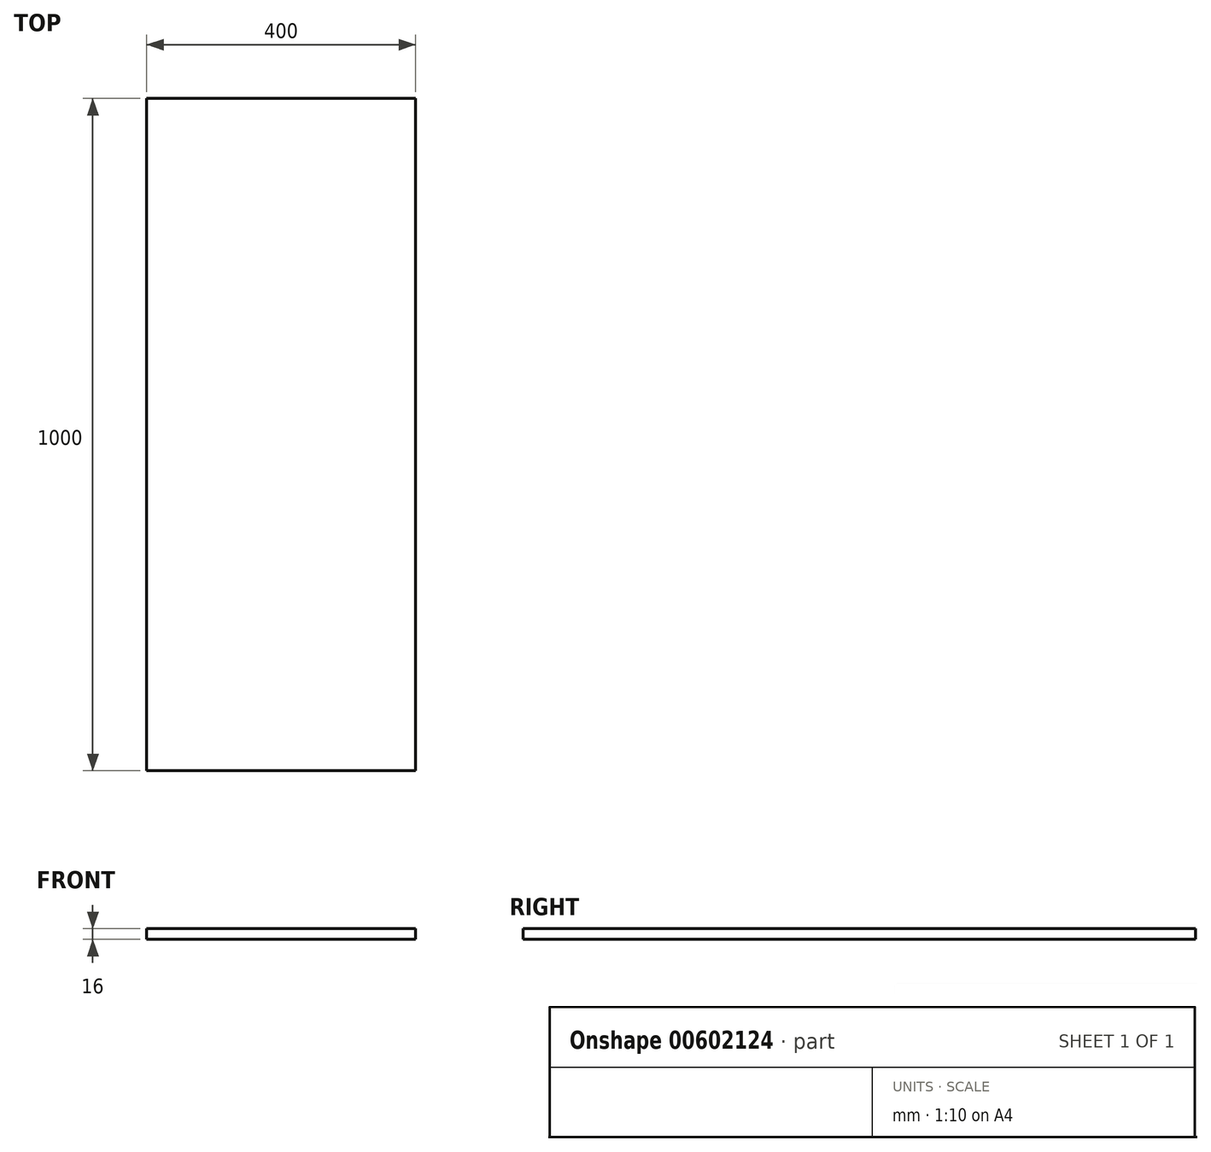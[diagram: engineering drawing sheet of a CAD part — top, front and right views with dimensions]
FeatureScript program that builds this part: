
annotation { "Feature Type Name" : "Feature", "Feature Type Description" : "" }
export const myFeature = defineFeature(function(context is Context, id is Id, definition is map)
    precondition{}
    {
        {
            var Q0;
            Q0=qCreatedBy(makeId("Top.planeOp"),FACE);
            var sketch = newSketch(context, id + "F0", { "sketchPlane" : qUnion([Q0])});
            skLineSegment(sketch, "E0.bottom", {"start": v(0, 0) * mm, "end": v(400, 0) * mm});
            skLineSegment(sketch, "E0.top", {"start": v(0, -1000) * mm, "end": v(400, -1000) * mm});
            skLineSegment(sketch, "E0.left", {"start": v(0, 0) * mm, "end": v(0, -1000) * mm});
            skLineSegment(sketch, "E0.right", {"start": v(400, 0) * mm, "end": v(400, -1000) * mm});
            skSolve(sketch);
        }
        {
            var Q0;
            Q0=qSketchRegion(id+"F0",true);
            extrude(context, id + "F1", {"entities" : qUnion([Q0]), "depth" : 16 * mm, "offsetDistance" : 25 * mm});
        }
    });
